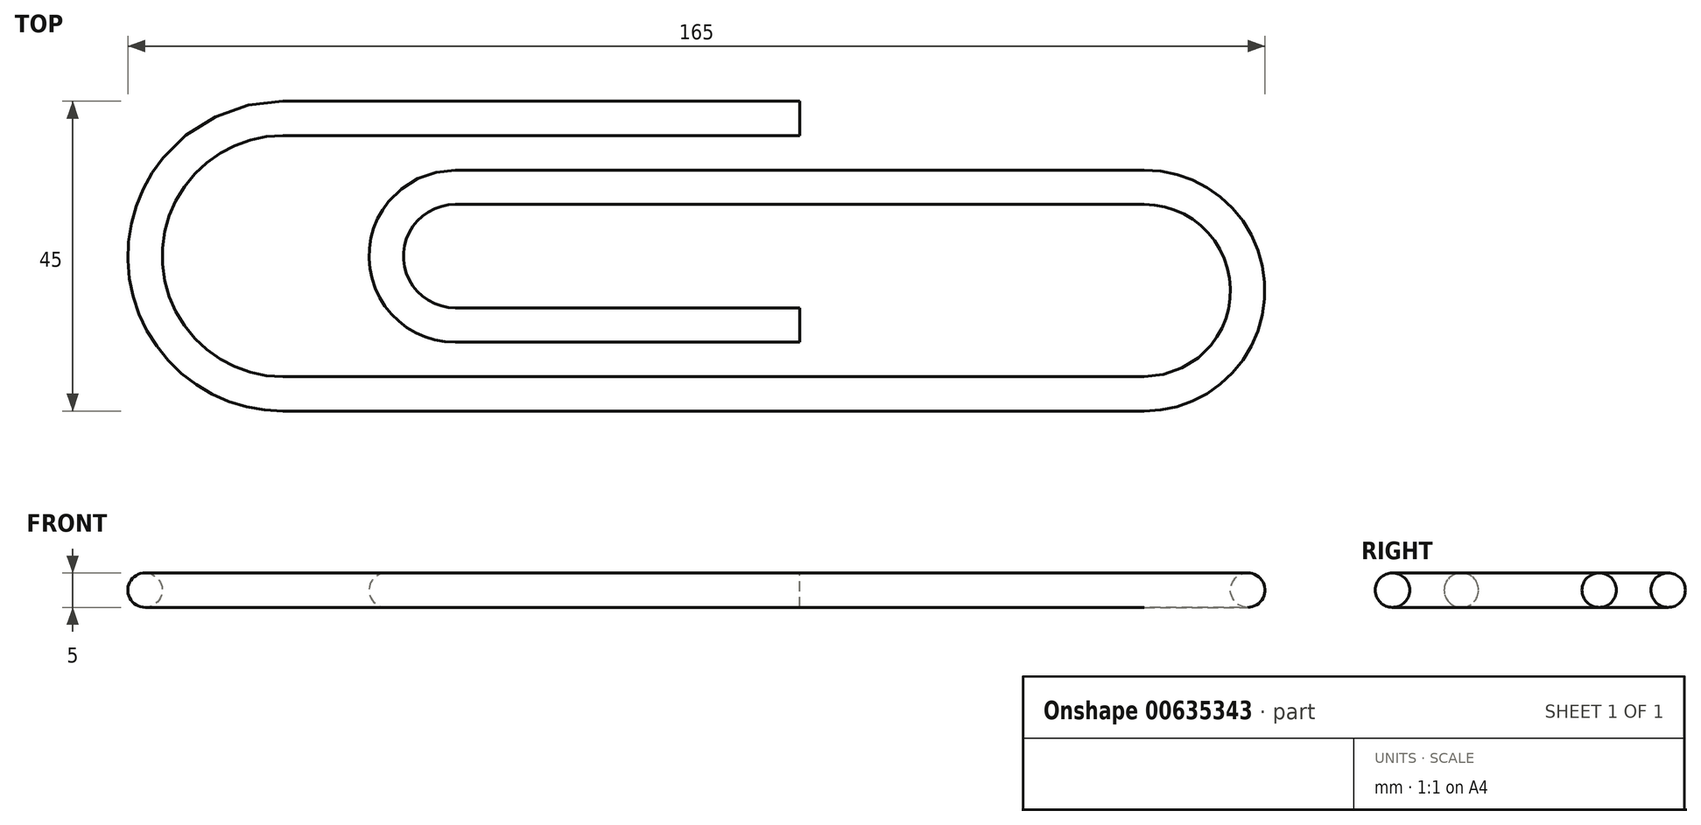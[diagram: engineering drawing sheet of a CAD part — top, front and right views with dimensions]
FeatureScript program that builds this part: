
annotation { "Feature Type Name" : "Feature", "Feature Type Description" : "" }
export const myFeature = defineFeature(function(context is Context, id is Id, definition is map)
    precondition{}
    {
        {
            var Q0;
            Q0=qCreatedBy(makeId("Top.planeOp"),FACE);
            var sketch = newSketch(context, id + "F0", { "sketchPlane" : qUnion([Q0])});
            skLineSegment(sketch, "E0", {"start": v(0, 0) * mm, "end": v(-75, 0) * mm});
            skArc(sketch, "E1", {"start": v(-75, 0) * mm, "mid": v(-95, -20) * mm, "end": v(-75, -40) * mm});
            skLineSegment(sketch, "E2", {"start": v(-75, -40) * mm, "end": v(50, -40) * mm});
            skArc(sketch, "E3", {"start": v(50, -40) * mm, "mid": v(65, -25) * mm, "end": v(50, -10) * mm});
            skLineSegment(sketch, "E4", {"start": v(50, -10) * mm, "end": v(-50, -10) * mm});
            skArc(sketch, "E5", {"start": v(-50, -10) * mm, "mid": v(-60, -20) * mm, "end": v(-50, -30) * mm});
            skLineSegment(sketch, "E6", {"start": v(-50, -30) * mm, "end": v(0, -30) * mm});
            skSolve(sketch);
        }
        {
            var Q0;
            Q0=qCreatedBy(makeId("Right.planeOp"),FACE);
            var sketch = newSketch(context, id + "F1", { "sketchPlane" : qUnion([Q0])});
            skCircle(sketch, "E7", {"center": v(0, 0) * mm, "radius": 2.5 * mm});
            skSolve(sketch);
        }
        {
            var Q0;
            Q0=qSketchRegion(id+"F1",true);
            var Q1;
            Q1=qConstructionFilter(qBodyType(qCreatedBy(id+"F0",EDGE),BodyType.WIRE),ConstructionObject.NO);
            sweep(context, id + "F2", {"profiles" : qUnion([Q0]), "path" : qUnion([Q1])});
        }
    });
